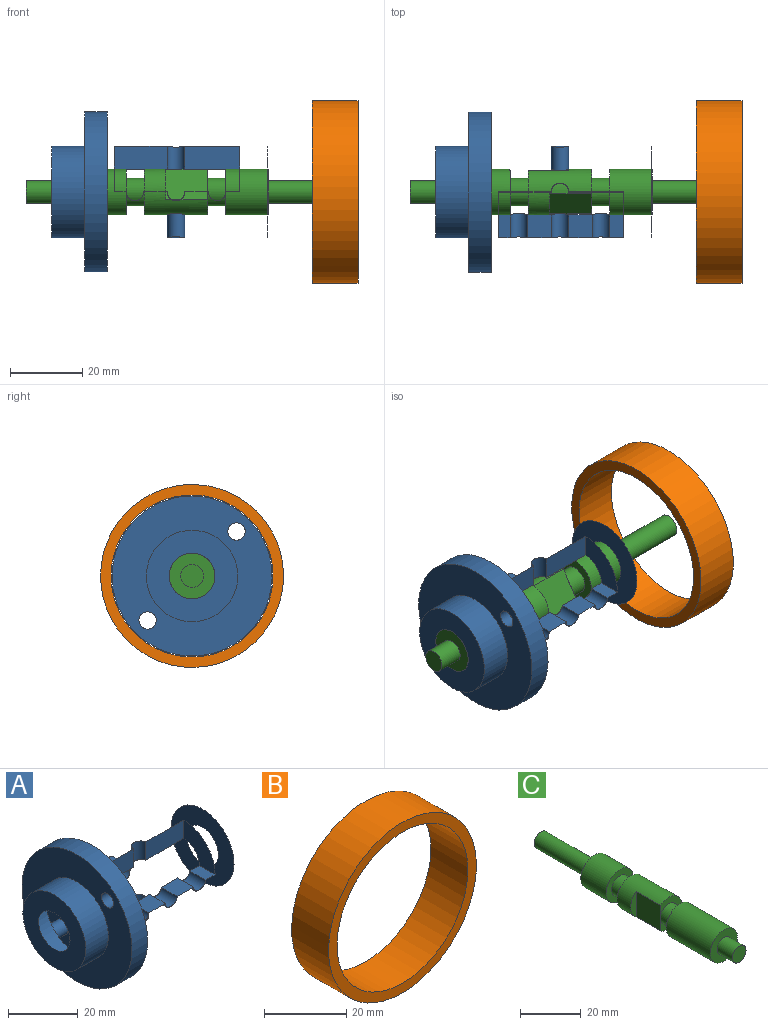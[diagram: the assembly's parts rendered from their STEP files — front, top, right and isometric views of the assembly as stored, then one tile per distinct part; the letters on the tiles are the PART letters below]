
ASSEMBLY  parts=3 mates=2
PART A: 28 faces, bbox 110.7x95.3x95.3 mm
  f0: cylinder r=2.41mm len=6.83mm, axis (0,-1,0), area 49.1mm2, adj f1,f2,f3,f4
  f1: cylinder r=6.35mm len=42.51mm, axis (-1,0,0), area 834mm2, adj f0,f2,f4,f5,f6,f7,f8,f9
  f2: plane 6.6x6.35mm, normal (0,0,1), area 41.9mm2, adj f0,f1,f3,f10
  f3: cylinder r=12.7mm len=42.51mm, axis (-1,0,0), area 795.9mm2, adj f0,f2,f4,f5,f6,f7,f8,f9
  f4: plane 6.6x6.35mm, normal (0,0,1), area 41.9mm2, adj f0,f1,f3,f11
  f5: cylinder r=2.41mm len=6.83mm, axis (0,0,1), area 49.1mm2, adj f1,f3,f6,f14
  f6: plane 66.14x57.15mm, normal (0,-1,0), area 97.4mm2, adj f1,f3,f5,f8
  f7: plane 25.4x25.4mm, normal (1,0,0), area 380mm2, adj f1,f3
  f8: plane 12.7x12.7mm, normal (-1,0,0), area 95mm2, adj f1,f3,f6,f9
  f9: plane 6.35x3.91mm, normal (0,0,1), area 24.8mm2, adj f1,f3,f8,f10
  f10: cylinder r=2.41mm len=6.83mm, axis (0,-1,0), area 49.1mm2, adj f1,f2,f3,f9
  f11: cylinder r=2.41mm len=6.83mm, axis (0,-1,0), area 49.1mm2, adj f1,f3,f4,f12
  f12: plane 6.35x3.27mm, normal (0,0,1), area 20.8mm2, adj f1,f3,f11,f13
  f13: plane 12.7x12.7mm, normal (1,0,0), area 95mm2, adj f1,f3,f12,f14
  f14: plane 40.1x31.75mm, normal (0,-1,0), area 93.3mm2, adj f1,f3,f5,f13
  f15: cylinder r=2.41mm len=6.83mm, axis (0,0,1), area 98.1mm2, adj f1,f17
  f16: cylinder r=2.41mm len=6.83mm, axis (0,-1,0), area 98.1mm2, adj f1,f18
  f17: cylinder r=12.7mm len=4.83mm, axis (-1,0,0), area 18.4mm2, adj f15
  f18: cylinder r=12.7mm len=4.83mm, axis (-1,0,0), area 18.4mm2, adj f16
  f19: plane 50.8x50.8mm, normal (1,0,0), area 380mm2, adj f20,f21
  f20: cylinder r=12.7mm len=25.4mm, axis (-1,0,0), area 729.7mm2, adj f19,f22
  f21: cylinder r=6.35mm len=12.7mm, axis (-1,0,0), area 0mm2, adj f19
  f22: plane 44.45x44.45mm, normal (1,0,0), area 1008.5mm2, adj f20,f23,f24,f25
  f23: cylinder r=2.41mm len=6.35mm, axis (-1,0,0), area 96.3mm2, adj f22,f26
  f24: cylinder r=2.41mm len=6.35mm, axis (-1,0,0), area 96.3mm2, adj f22,f26
  f25: cylinder r=22.23mm len=44.45mm, axis (-1,0,0), area 886.7mm2, adj f22,f26
  f26: plane 95.25x95.25mm, normal (-1,0,0), area 1008.5mm2, adj f23,f24,f25,f27
  f27: cylinder r=12.7mm len=25.4mm, axis (-1,0,0), area 0mm2, adj f26
PART B: 4 faces, bbox 50.8x12.7x50.8 mm
  f0: cylinder r=22.5mm len=45mm, axis (0,1,0), area 1795.4mm2, adj f2,f3
  f1: cylinder r=25.4mm len=50.8mm, axis (0,1,0), area 2026.8mm2, adj f2,f3
  f2: plane 50.8x50.8mm, normal (0,-1,0), area 436.4mm2, adj f0,f1
  f3: plane 50.8x50.8mm, normal (0,1,0), area 436.4mm2, adj f0,f1
PART C: 21 faces, bbox 12.7x92.2x12.7 mm
  f0: cylinder r=6.35mm len=20.7mm, axis (0,-1,0), area 823.1mm2, adj f3,f8,f14,f15
  f1: cylinder r=6.35mm len=17.53mm, axis (0,-1,0), area 430.4mm2, adj f2,f7,f12,f13,f16,f17
  f2: plane 12.7x10.16mm, normal (0,1,0), area 63mm2, adj f1,f9,f13
  f3: plane 12.7x12.7mm, normal (0,-1,0), area 95mm2, adj f0,f4
  f4: cylinder r=3.17mm len=7.11mm, axis (0,1,0), area 141.9mm2, adj f3,f5
  f5: plane 6.35x6.35mm, normal (0,-1,0), area 31.7mm2, adj f4
  f6: cylinder r=3.81mm len=7.62mm, axis (0,-1,0), area 121.6mm2, adj f7,f8
  f7: plane 12.7x10.16mm, normal (0,-1,0), area 63mm2, adj f1,f6,f16
  f8: plane 12.7x10.16mm, normal (0,1,0), area 63mm2, adj f0,f6,f14
  f9: cylinder r=3.81mm len=7.62mm, axis (0,1,0), area 121.6mm2, adj f2,f10
  f10: plane 12.7x12.7mm, normal (0,-1,0), area 81.1mm2, adj f9,f11
  f11: cylinder r=6.35mm len=12.7mm, axis (0,-1,0), area 471.2mm2, adj f10,f19
  f12: plane 10.16x2.54mm, normal (0,1,0), area 18mm2, adj f1,f13
  f13: plane 11.64x10.16mm, normal (1,0,0), area 118.3mm2, adj f1,f2,f12
  f14: plane 10.16x0.24mm, normal (-1,0,0), area 2.5mm2, adj f0,f8,f15
  f15: plane 10.16x2.54mm, normal (0,1,0), area 18mm2, adj f0,f14
  f16: plane 11.19x10.16mm, normal (-1,0,0), area 113.7mm2, adj f1,f7,f17
  f17: plane 10.16x2.54mm, normal (0,-1,0), area 18mm2, adj f1,f16
  f18: cylinder r=3.17mm len=24.89mm, axis (0,-1,0), area 496.6mm2, adj f19,f20
  f19: plane 12.7x12.7mm, normal (0,1,0), area 95mm2, adj f11,f18
  f20: plane 6.35x6.35mm, normal (0,1,0), area 31.7mm2, adj f18
PLACE A t=(4.39,2.65,-11.73)mm fixed
PLACE B rot(axis=(0.69,-0.69,0.2),156.9deg) t=(76.78,2.65,-11.73)mm
PLACE C rot(axis=(-0.27,-0.27,-0.92),94.6deg) t=(4.39,2.65,-11.73)mm
MATE fastened B.f1 <-> C.f4  axis (1,0,0) through (89.48,2.65,-11.73)mm
MATE revolute C.f0 <-> A.f1  axis (-1,0,0) through (4.39,2.65,-11.73)mm
